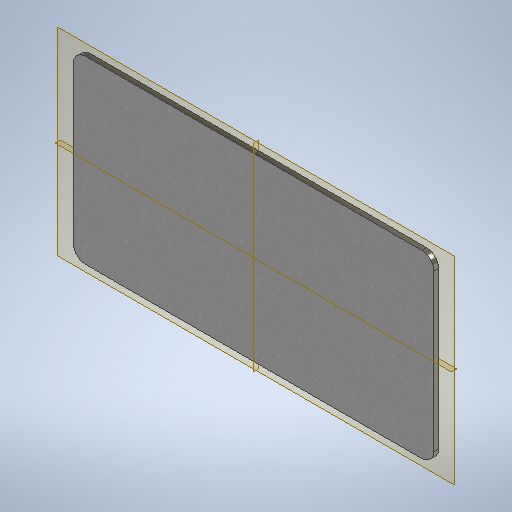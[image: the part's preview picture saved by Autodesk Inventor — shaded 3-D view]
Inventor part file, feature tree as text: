
AUTODESK INVENTOR PART (.ipt)
format: ipt  version: 2025.2 (Build 292293000, 293)  size: 299,008 bytes
history: native  units: mm
features: fillet x3, other x2, sheet_metal_op x1, sketch x1
ambient origin geometry x8: Origin, YZ Plane, XZ Plane, XY Plane, X Axis, Y Axis, Z Axis, Center Point
bodies: Body1 (feature_tree)
feature tree (7):
  other  "Sólido1"
  sheet_metal_op  "Face1"
  fillet  "Arredondamento1"  Radius=1500.0mm
  fillet  "Arredondamento2"  Radius=750.0mm
  fillet  "Arredondamento3"  Radius=20.0mm
  sketch  "Esboço1"  dims[d3=50.0mm d4=50.0mm d5=50.0mm]
  other  "Placa1"
